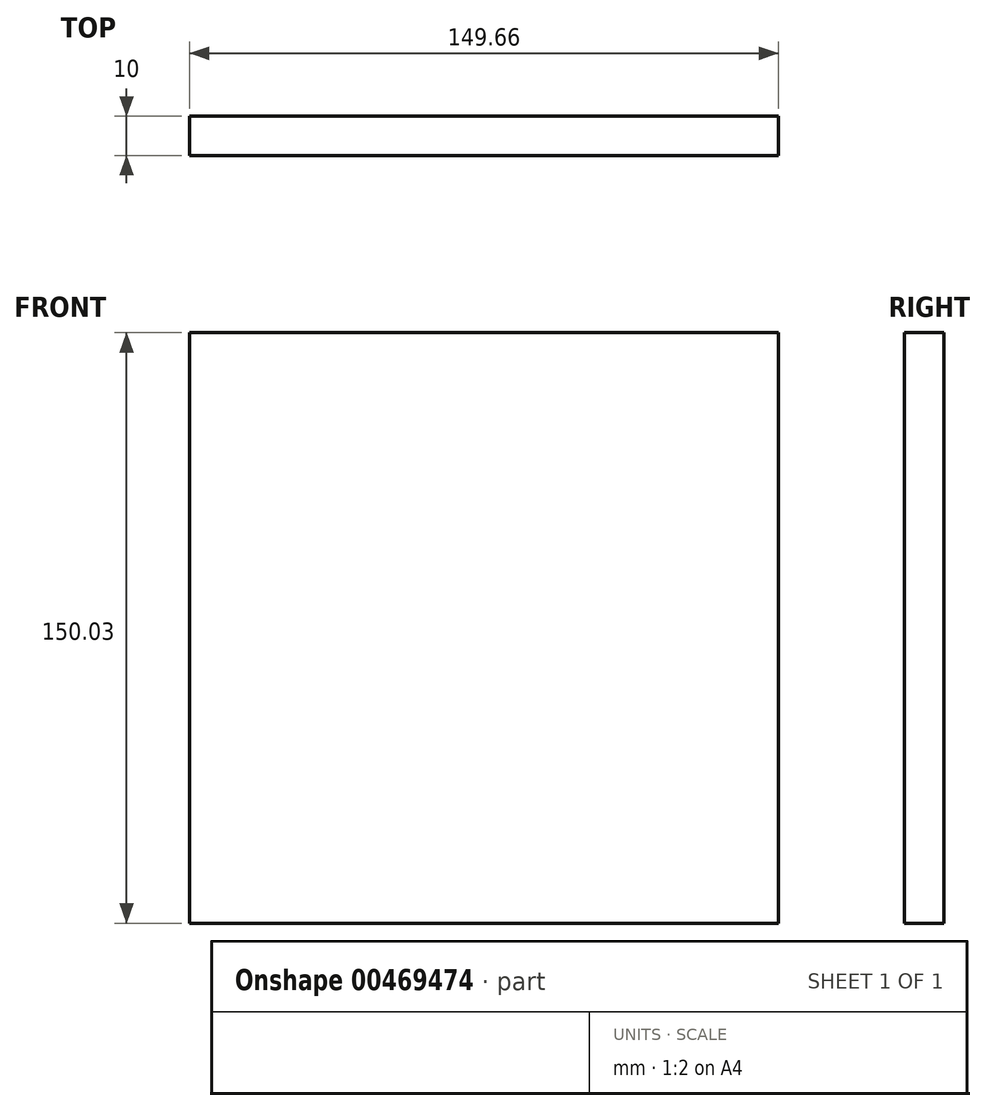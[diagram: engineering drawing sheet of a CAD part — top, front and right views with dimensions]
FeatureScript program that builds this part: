
annotation { "Feature Type Name" : "Feature", "Feature Type Description" : "" }
export const myFeature = defineFeature(function(context is Context, id is Id, definition is map)
    precondition{}
    {
        {
            var Q0;
            Q0=qCreatedBy(makeId("Front.planeOp"),FACE);
            var sketch = newSketch(context, id + "F0", { "sketchPlane" : qUnion([Q0])});
            skLineSegment(sketch, "E0.bottom", {"start": v(-74.74, 75.2) * mm, "end": v(74.92, 75.2) * mm});
            skLineSegment(sketch, "E0.top", {"start": v(-74.74, -74.83) * mm, "end": v(74.92, -74.83) * mm});
            skLineSegment(sketch, "E0.left", {"start": v(-74.74, 75.2) * mm, "end": v(-74.74, -74.83) * mm});
            skLineSegment(sketch, "E0.right", {"start": v(74.92, 75.2) * mm, "end": v(74.92, -74.83) * mm});
            skSolve(sketch);
        }
        {
            var Q0;
            Q0=makeQuery(id+"F0.imprint","IMPRINT",FACE,{"disambiguationData":[TD([[makeQuery(id+"F0.imprint","IMPRINT",EDGE,{"derivedFrom":sQuery(id+"F0.wireOp",EDGE,"E0.bottom")}),-1.0]])]});
            extrude(context, id + "F1", {"entities" : qUnion([Q0]), "depth" : 10 * mm});
        }
    });
